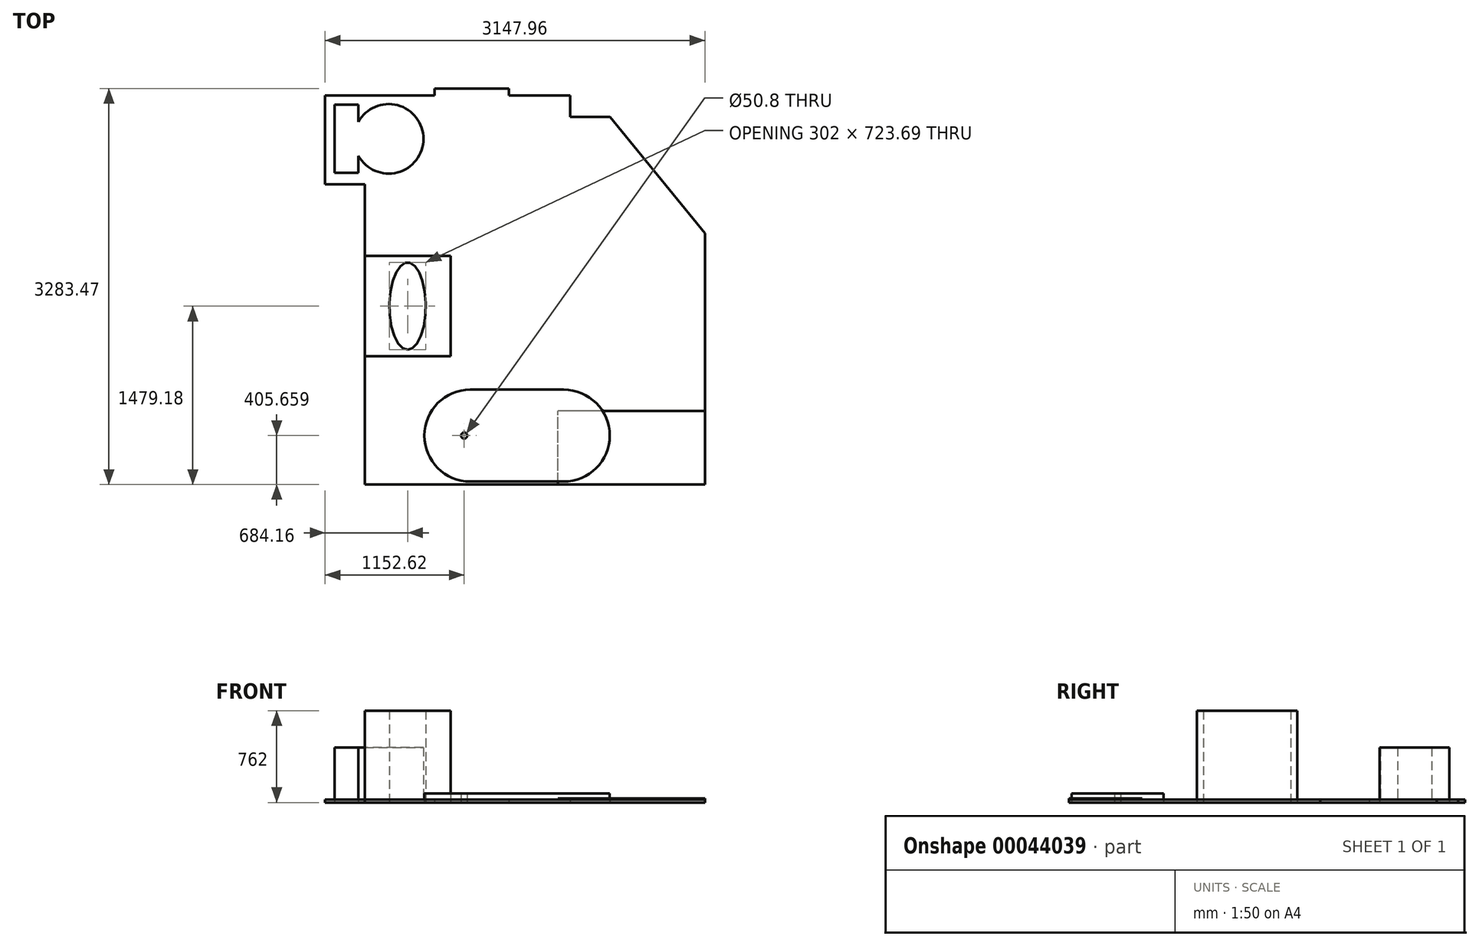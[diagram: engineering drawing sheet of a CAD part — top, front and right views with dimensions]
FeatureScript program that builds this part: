
annotation { "Feature Type Name" : "Feature", "Feature Type Description" : "" }
export const myFeature = defineFeature(function(context is Context, id is Id, definition is map)
    precondition{}
    {
        {
            var Q0;
            Q0=qCreatedBy(makeId("Top.planeOp"),FACE);
            var sketch = newSketch(context, id + "F0", { "sketchPlane" : qUnion([Q0])});
            skLineSegment(sketch, "E0", {"start": v(0, 0) * mm, "end": v(-1803.4, 0) * mm});
            skLineSegment(sketch, "E1", {"start": v(-1803.4, 0) * mm, "end": v(-1803.4, 2489.2) * mm});
            skLineSegment(sketch, "E2", {"start": v(-1803.4, 2489.2) * mm, "end": v(-2131.96, 2489.2) * mm});
            skLineSegment(sketch, "E3", {"start": v(-2131.96, 2489.2) * mm, "end": v(-2131.96, 3225.8) * mm});
            skLineSegment(sketch, "E4", {"start": v(-2131.96, 3225.8) * mm, "end": v(-1225.8, 3225.8) * mm});
            skLineSegment(sketch, "E5", {"start": v(-99.96, 3225.8) * mm, "end": v(-99.96, 3048) * mm});
            skLineSegment(sketch, "E6", {"start": v(-99.96, 3048) * mm, "end": v(230.24, 3048) * mm});
            skLineSegment(sketch, "E7", {"start": v(230.24, 3048) * mm, "end": v(1016, 2082.8) * mm});
            skLineSegment(sketch, "E8", {"start": v(1016, 2082.8) * mm, "end": v(1016, 0) * mm});
            skLineSegment(sketch, "E9", {"start": v(1016, 0) * mm, "end": v(0, 0) * mm});
            skLineSegment(sketch, "E10", {"start": v(-608.88, 3225.8) * mm, "end": v(-608.88, 3283.47) * mm});
            skLineSegment(sketch, "E11", {"start": v(-608.88, 3283.47) * mm, "end": v(-1225.8, 3283.47) * mm});
            skLineSegment(sketch, "E12", {"start": v(-1225.8, 3283.47) * mm, "end": v(-1225.8, 3225.8) * mm});
            skLineSegment(sketch, "E13.trimOffspring", {"start": v(-608.88, 3225.8) * mm, "end": v(-99.96, 3225.8) * mm});
            skSolve(sketch);
        }
        {
            var Q0;
            Q0=makeQuery(id+"F0.imprint","IMPRINT",FACE,{"disambiguationData":[TD([[makeQuery(id+"F0.imprint","IMPRINT",EDGE,{"derivedFrom":sQuery(id+"F0.wireOp",EDGE,"E0")}),-1.0]])]});
            extrude(context, id + "F1", {"entities" : qUnion([Q0]), "depth" : 25.4 * mm});
        }
        {
            var Q0;
            Q0=makeQuery(id+"F1.opExtrude","CAP_FACE",FACE,{"disambiguationData":[OSD([sQuery(id+"F0.wireOp",EDGE,"E0"),sQuery(id+"F0.wireOp",EDGE,"E1"),sQuery(id+"F0.wireOp",EDGE,"E2"),sQuery(id+"F0.wireOp",EDGE,"E3"),sQuery(id+"F0.wireOp",EDGE,"E4"),sQuery(id+"F0.wireOp",EDGE,"E5"),sQuery(id+"F0.wireOp",EDGE,"E6"),sQuery(id+"F0.wireOp",EDGE,"E7"),sQuery(id+"F0.wireOp",EDGE,"E8"),sQuery(id+"F0.wireOp",EDGE,"E9")])],"isStart":false});
            var sketch = newSketch(context, id + "F2", { "sketchPlane" : qUnion([Q0])});
            skLineSegment(sketch, "E14.bottom", {"start": v(1016, 0) * mm, "end": v(-203.2, 0) * mm});
            skLineSegment(sketch, "E14.top", {"start": v(1016, 609.6) * mm, "end": v(-203.2, 609.6) * mm});
            skLineSegment(sketch, "E14.left", {"start": v(1016, 0) * mm, "end": v(1016, 609.6) * mm});
            skLineSegment(sketch, "E14.right", {"start": v(-203.2, 0) * mm, "end": v(-203.2, 609.6) * mm});
            skSolve(sketch);
        }
        {
            var Q0;
            Q0 = qSketchRegion(id + "F2", true);
            extrude(context, id + "F3", {"entities" : qUnion([Q0]), "depth" : 9.52 * mm});
        }
        {
            var Q0;
            Q0=qCreatedBy(makeId("Top.planeOp"),FACE);
            var sketch = newSketch(context, id + "F4", { "sketchPlane" : qUnion([Q0])});
            skLineSegment(sketch, "E15.rect.bottom", {"start": v(-153.84, 786.66) * mm, "end": v(-928.54, 786.66) * mm});
            skLineSegment(sketch, "E15.rect.top", {"start": v(-153.84, 24.66) * mm, "end": v(-928.54, 24.66) * mm});
            skLineSegment(sketch, "E15.rect.left", {"start": v(-153.84, 786.66) * mm, "end": v(-153.84, 24.66) * mm});
            skLineSegment(sketch, "E15.rect.right", {"start": v(-928.54, 786.66) * mm, "end": v(-928.54, 24.66) * mm});
            skPoint(sketch, "E15.rect.middle", {"position": v(-541.19, 405.66) * mm});
            skArc(sketch, "E16", {"start": v(-928.54, 786.66) * mm, "mid": v(-1309.54, 405.66) * mm, "end": v(-928.54, 24.66) * mm});
            skArc(sketch, "E17", {"start": v(-153.84, 24.66) * mm, "mid": v(227.16, 405.66) * mm, "end": v(-153.84, 786.66) * mm});
            skCircle(sketch, "E18", {"center": v(-979.34, 405.66) * mm, "radius": 25.4 * mm});
            skSolve(sketch);
        }
        {
            var Q0;
            Q0 = qSketchRegion(id + "F4", true);
            extrude(context, id + "F5", {"entities" : qUnion([Q0]), "depth" : 76.2 * mm});
        }
        {
            var Q0;
            Q0=qCreatedBy(makeId("Top.planeOp"),FACE);
            var sketch = newSketch(context, id + "F6", { "sketchPlane" : qUnion([Q0])});
            skLineSegment(sketch, "E19.rect.bottom", {"start": v(-1855.75, 2583.52) * mm, "end": v(-2053.73, 2583.52) * mm});
            skLineSegment(sketch, "E19.rect.top", {"start": v(-1855.75, 3149.2) * mm, "end": v(-2053.73, 3149.2) * mm});
            skLineSegment(sketch, "E19.rect.left", {"start": v(-1855.75, 2583.52) * mm, "end": v(-1855.75, 3149.2) * mm});
            skLineSegment(sketch, "E19.rect.right", {"start": v(-2053.73, 2583.52) * mm, "end": v(-2053.73, 3149.2) * mm});
            skPoint(sketch, "E19.rect.middle", {"position": v(-1954.74, 2866.35) * mm});
            skArc(sketch, "E20", {"start": v(-1855.75, 2724.94) * mm, "mid": v(-1316.18, 2866.35) * mm, "end": v(-1855.75, 3007.77) * mm});
            skSolve(sketch);
        }
        {
            var Q0;
            Q0 = qSketchRegion(id + "F6", true);
            extrude(context, id + "F7", {"entities" : qUnion([Q0]), "depth" : 457.2 * mm});
        }
        {
            var Q0;
            Q0=qCreatedBy(makeId("Top.planeOp"),FACE);
            var sketch = newSketch(context, id + "F8", { "sketchPlane" : qUnion([Q0])});
            skLineSegment(sketch, "E21.0", {"start": v(-1803.4, 0) * mm, "end": v(-1803.4, 2489.2) * mm});
            skLineSegment(sketch, "E22.bottom", {"start": v(-1803.4, 1895.1) * mm, "end": v(-1092.2, 1895.1) * mm});
            skLineSegment(sketch, "E22.top", {"start": v(-1803.4, 1063.26) * mm, "end": v(-1092.2, 1063.26) * mm});
            skLineSegment(sketch, "E22.left", {"start": v(-1803.4, 1895.1) * mm, "end": v(-1803.4, 1063.26) * mm});
            skLineSegment(sketch, "E22.right", {"start": v(-1092.2, 1895.1) * mm, "end": v(-1092.2, 1063.26) * mm});
            skEllipse(sketch, "E23", {"center": v(-1447.8, 1479.18) * mm, "majorRadius": 361.85 * mm, "minorRadius": 151 * mm, "majorAxis": v(0, -1)});
            skPoint(sketch, "E23.centerSnap0", {"position": v(-1092.2, 1479.18) * mm});
            skPoint(sketch, "E23.centerSnap1", {"position": v(-1447.8, 1063.26) * mm});
            skSolve(sketch);
        }
        {
            var Q0;
            Q0=makeQuery(id+"F8.imprint","IMPRINT",FACE,{"disambiguationData":[TD([[makeQuery(id+"F8.imprint","IMPRINT",EDGE,{"derivedFrom":sQuery(id+"F8.wireOp",EDGE,"E22.bottom")}),-1.0]])]});
            extrude(context, id + "F9", {"entities" : qUnion([Q0]), "depth" : 762 * mm});
        }
    });
